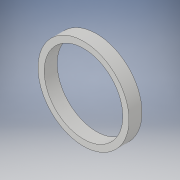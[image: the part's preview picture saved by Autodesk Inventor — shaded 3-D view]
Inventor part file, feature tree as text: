
AUTODESK INVENTOR PART (.ipt)
format: ipt  version: 2019 (Build 230136000, 136)  size: 104,960 bytes
history: native  units: mm
features: extrude x2, sketch x2
ambient origin geometry x8: Origin, YZ Plane, XZ Plane, XY Plane, X Axis, Y Axis, Z Axis, Center Point
bodies: Solid1 (feature_tree)
feature tree (4):
  extrude  "Extrusion1"  Depth=10.0mm TaperAngle=0.0deg
  extrude  "Extrusion2"  Depth=10.0mm TaperAngle=0.0deg
  sketch  "Sketch1"  dims[d0=70.0mm d1=10.0mm d2=0.0mm]
  sketch  "Sketch2"  dims[d3=60.5mm d4=10.0mm d5=0.0mm]
